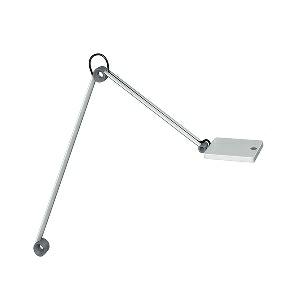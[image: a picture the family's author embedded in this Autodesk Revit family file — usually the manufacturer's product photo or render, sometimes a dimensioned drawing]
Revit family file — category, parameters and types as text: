
# Revit family: para_mi_-_ftl_108_r__940_00644097_73b1
name_source: partatom
category: Lighting Fixtures
units: mm (PartAtom-declared; Revit-internal decimal feet)

## family parameters
Cut with Voids When Loaded = No
Host = Face
Light Source = No
Part Type = Normal
Room Calculation Point = No
Round Connector Dimension = Use Diameter
Shared = No

## types (1)
- PARA.MI - FTL 108 R /940 (1 x LED, 600 lm, 4000K)
    Apparent Load = 7 VA
    Approval mark = CE
    CIE Flux Codes = 70 94 99 100 100
    Color Rendering = 90-100
    Color Temperature = 4000K
    Control Gear = Electronic ballast
    Default Elevation = 1800 mm
    Description = FTL 108 R|Task luminaire|light source: LED|work equipment: Electronic plug-in transformer|connected load: 100-240 V, 50/60 Hz|Power consumption: approx. 7 W|luminous flux: 600 lm|luminous efficacy: 85 lm/W|Illuminance efficiency factor: 111 lx/W|colour temperature: Cold white, ca. 4000 K|color rendering index (CRI): >= 90|chromaticity tolerance:  3 SDCM|class of protection: II with plug-in power supply, III without plug-in power supply|technology: Continuously dimmable|luminaire body|material: Aluminium|surface: Painted|colour: Silver|lamp cover: Plastic, Clear|tubular sections|material: Tubular aluminium section|surface: Painted|colour: Silver metallic|weight (net): approx. 1.0 kg|mains lead: 3.00 m Mains plug BS 1363, CEE 7/XVI, NEMA 1-15P|Fastening: Adaptor (accessory), Table base (accessory), Table clamp (accessory), Tap16|glare control: Reflector|special features: Automatic switchoff adjustable, Push button in luminaire head, Behaviour at net recovery adjustable|Approval mark: C - ETL - US (F. CAN U. USA), VDE - ENEC SEP LIGHT & POWER SUPPLY UNIT|
    Height = 12 mm  [stored 0.0393701 ft]
    Lamp = 1 x LED
    Lamp Light Flux = 600 lm
    Lamp count = 1
    Length = 123 mm
    Luminous efficacy = 86 lm/W
    Manufacturer = Waldmann
    ModVariant = No
    Model = 00644097
    Mounting Place = Table
    Mounting Type = Surface mounted
    Number of Poles = 1
    OnlyDefault = Yes
    Power Factor = 1
    Product Name = PARA.MI - FTL 108 R /940
    Product group = Task luminaire (office)
    ProductGroupID = 21
    Protection Class = Protection class II
    Protection Degree = IP 40
    RLX_Detail_Level = 1
    RLX_Emergency_Light_Flux = 0 lm
    RLX_Emergency_Type = 0
    RLX_Emergency_Type_DB = No
    RlxData = <blob elided: 70313 chars, md5=0e605f3c>
    Socket = socket
    Standby Power = 0 W
    System Light Flux = 600 lm
    System Power = 7 W
    Type Comments = Product without accessories
    Type Image = 113148000-00644097.jpg
    URL = http://relux.com
    VarID = ---
    Voltage = 230 V
    Voltage Range = 220-240 V
    Weight = 0.00 kg
    Width = 0 mm  [stored 0 ft]

note: [stored X ft] marks values corroborated as IEEE doubles in the binary element streams (Revit-internal decimal feet)

## geometry (parser evidence)
native form markers: Blend x4, Sweep x12
no freeform markers — native parametric forms only
